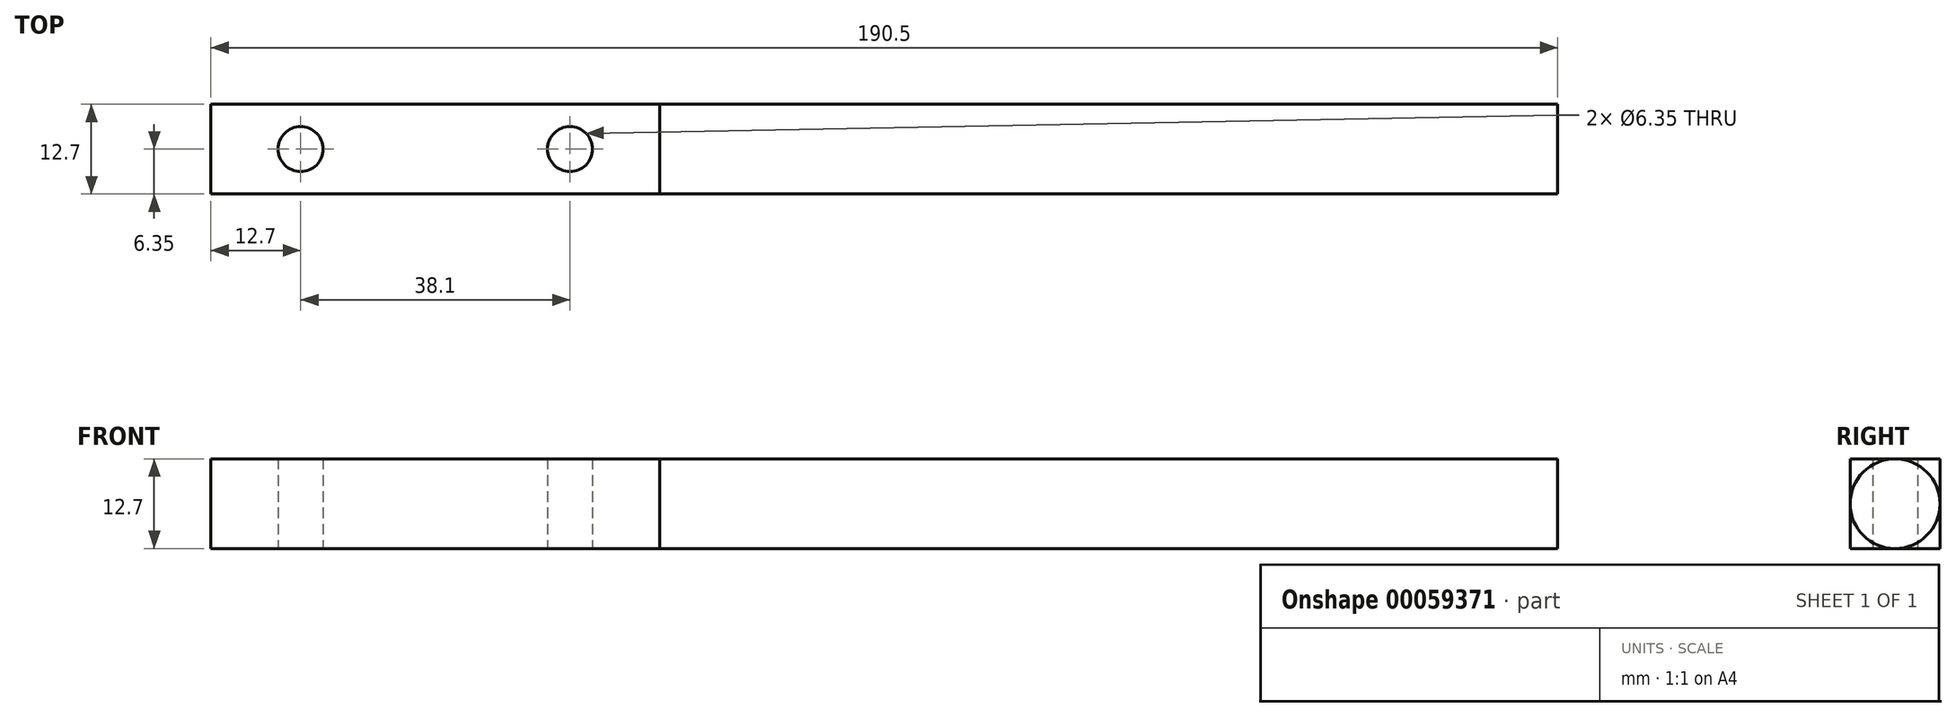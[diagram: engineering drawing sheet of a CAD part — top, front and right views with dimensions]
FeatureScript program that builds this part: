
annotation { "Feature Type Name" : "Feature", "Feature Type Description" : "" }
export const myFeature = defineFeature(function(context is Context, id is Id, definition is map)
    precondition{}
    {
        {
            var Q0;
            Q0=qCreatedBy(makeId("Top.planeOp"),FACE);
            var sketch = newSketch(context, id + "F0", { "sketchPlane" : qUnion([Q0])});
            skLineSegment(sketch, "E0", {"start": v(0, 0) * mm, "end": v(0, 6.35) * mm});
            skLineSegment(sketch, "E1", {"start": v(0, 6.35) * mm, "end": v(-63.5, 6.35) * mm});
            skLineSegment(sketch, "E2", {"start": v(-63.5, 6.35) * mm, "end": v(-63.5, -6.35) * mm});
            skLineSegment(sketch, "E3", {"start": v(-63.5, -6.35) * mm, "end": v(0, -6.35) * mm});
            skLineSegment(sketch, "E4", {"start": v(0, -6.35) * mm, "end": v(0, 0) * mm});
            skLineSegment(sketch, "E5.0", {"start": v(-12.7, 6.35) * mm, "end": v(-12.7, -6.35) * mm});
            skCircle(sketch, "E6", {"center": v(-12.7, 0) * mm, "radius": 3.18 * mm});
            skLineSegment(sketch, "E7.0", {"start": v(-50.8, 0) * mm, "end": v(-50.8, 6.35) * mm});
            skCircle(sketch, "E8", {"center": v(-50.8, 0) * mm, "radius": 3.18 * mm});
            skSolve(sketch);
        }
        {
            var Q0;
            {var subQ1=sQuery(id+"F0.wireOp",EDGE,"E2");Q0=makeQuery(id+"F0.imprint","IMPRINT",FACE,{"disambiguationData":[TD([[makeQuery(id+"F0.imprint","IMPRINT",EDGE,{"derivedFrom":subQ1}),1.0]])]});}
            var Q1;
            {var subQ5=sQuery(id+"F0.wireOp",EDGE,"E0");Q1=makeQuery(id+"F0.imprint","IMPRINT",FACE,{"disambiguationData":[TD([[makeQuery(id+"F0.imprint","IMPRINT",EDGE,{"derivedFrom":subQ5}),1.0]])]});}
            extrude(context, id + "F1", {"entities" : qUnion([Q0, Q1]), "endBound" : BoundingType.SYMMETRIC, "depth" : 12.7 * mm});
        }
        {
            var Q0;
            Q0=makeQuery(id+"F1.opExtrude","SWEPT_FACE",FACE,{"disambiguationData":[OSD([sQuery(id+"F0.wireOp",EDGE,"E0"),sQuery(id+"F0.wireOp",EDGE,"E4")])]});
            var sketch = newSketch(context, id + "F2", { "sketchPlane" : qUnion([Q0])});
            skCircle(sketch, "E9", {"center": v(0, 0) * mm, "radius": 6.35 * mm});
            skSolve(sketch);
        }
        {
            var Q0;
            {var subQ0=sQuery(id+"F2.wireOp",EDGE,"E9");var subQ1=sQuery(id+"F0.wireOp",EDGE,"E4");var subQ2=sQuery(id+"F0.wireOp",EDGE,"E0");var subQ3=makeQuery(id+"F2.imprint","INTERSECT",VERTEX,{"derivedFrom":[makeQuery(id+"F1.opExtrude","CAP_EDGE",EDGE,{"disambiguationData":[OSD([subQ2,subQ1])],"isStart":false}),subQ0]});Q0=makeQuery(id+"F2.imprint","IMPRINT",FACE,{"disambiguationData":[TD([[makeQuery(id+"F2.imprint","IMPRINT",EDGE,{"disambiguationData":[TD([[subQ3,1.0]])],"derivedFrom":subQ0}),1.0]])]});}
            extrude(context, id + "F3", {"entities" : qUnion([Q0]), "operationType" : NewBodyOperationType.ADD, "depth" : 127 * mm});
        }
    });
